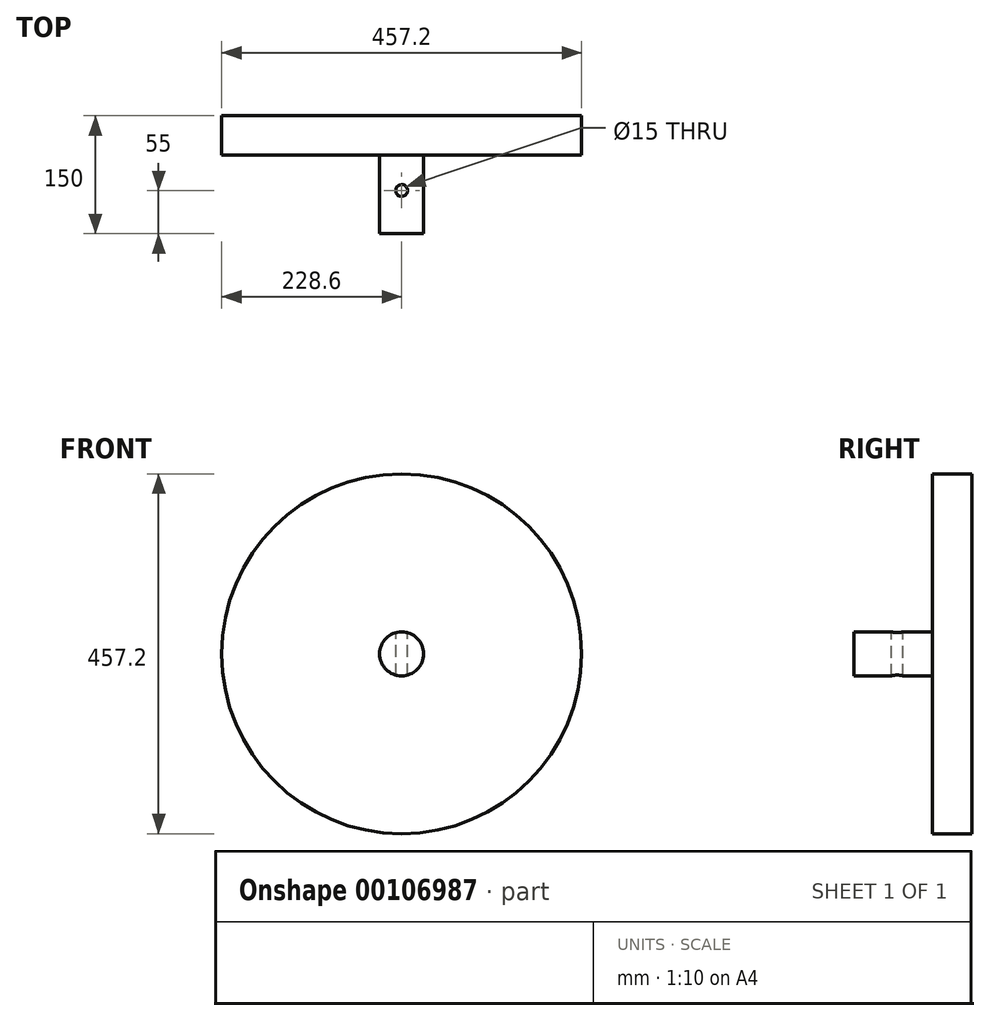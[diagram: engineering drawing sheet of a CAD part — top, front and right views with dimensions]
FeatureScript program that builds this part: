
annotation { "Feature Type Name" : "Feature", "Feature Type Description" : "" }
export const myFeature = defineFeature(function(context is Context, id is Id, definition is map)
    precondition{}
    {
        {
            var Q0;
            Q0=qCreatedBy(makeId("Front.planeOp"),FACE);
            var sketch = newSketch(context, id + "F0", { "sketchPlane" : qUnion([Q0])});
            skCircle(sketch, "E0", {"center": v(0, 0) * mm, "radius": 228.6 * mm});
            skSolve(sketch);
        }
        {
            var Q0;
            Q0=qCreatedBy(makeId("Front.planeOp"),FACE);
            var sketch = newSketch(context, id + "F1", { "sketchPlane" : qUnion([Q0])});
            skCircle(sketch, "E1", {"center": v(0, 0) * mm, "radius": 28 * mm});
            skSolve(sketch);
        }
        {
            var Q0;
            Q0=makeQuery(id+"F1.imprint","IMPRINT",FACE,{"disambiguationData":[TD([[makeQuery(id+"F1.imprint","IMPRINT",EDGE,{"derivedFrom":sQuery(id+"F1.wireOp",EDGE,"E1")}),1.0]])]});
            var Q1;
            Q1=sQuery(id+"F1.wireOp",EDGE,"E1");
            extrude(context, id + "F2", {"entities" : qUnion([Q0]), "surfaceEntities" : qUnion([Q1]), "depth" : 100 * mm});
        }
        {
            var Q0;
            Q0=makeQuery(id+"F0.imprint","IMPRINT",FACE,{"disambiguationData":[TD([[makeQuery(id+"F0.imprint","IMPRINT",EDGE,{"derivedFrom":sQuery(id+"F0.wireOp",EDGE,"E0")}),1.0]])]});
            var Q1;
            Q1=sQuery(id+"F0.wireOp",EDGE,"E0");
            extrude(context, id + "F3", {"entities" : qUnion([Q0]), "operationType" : NewBodyOperationType.ADD, "surfaceEntities" : qUnion([Q1]), "oppositeDirection" : true, "depth" : 50 * mm});
        }
        {
            var Q0;
            Q0=qCreatedBy(makeId("Top.planeOp"),FACE);
            var sketch = newSketch(context, id + "F4", { "sketchPlane" : qUnion([Q0])});
            skLineSegment(sketch, "E2", {"start": v(0, 0) * mm, "end": v(0, -100) * mm, "construction": true});
            skCircle(sketch, "E3", {"center": v(0, -45) * mm, "radius": 7.5 * mm});
            skSolve(sketch);
        }
        {
            var Q0;
            Q0 = qSketchRegion(id + "F4", true);
            var Q1;
            Q1=sQuery(id+"F4.wireOp",EDGE,"E3");
            extrude(context, id + "F5", {"entities" : qUnion([Q0]), "operationType" : NewBodyOperationType.REMOVE, "surfaceEntities" : qUnion([Q1]), "endBound" : BoundingType.UP_TO_NEXT, "oppositeDirection" : true, "depth" : 25 * mm, "hasSecondDirection" : true, "secondDirectionBound" : SecondDirectionBoundingType.UP_TO_NEXT, "secondDirectionOppositeDirection" : false, "secondDirectionDepth" : 25 * mm});
        }
    });
